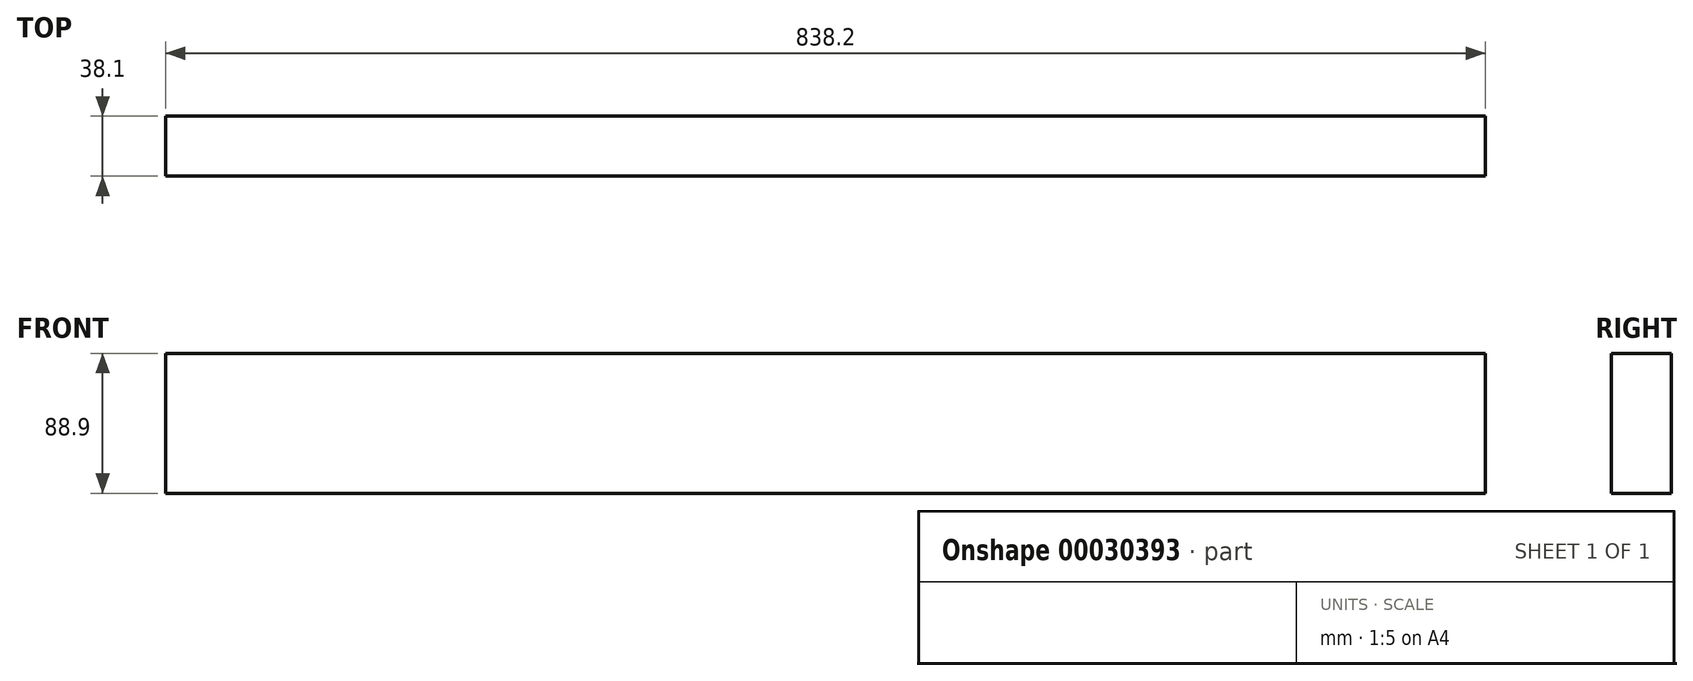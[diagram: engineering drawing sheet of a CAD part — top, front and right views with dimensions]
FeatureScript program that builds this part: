
annotation { "Feature Type Name" : "Feature", "Feature Type Description" : "" }
export const myFeature = defineFeature(function(context is Context, id is Id, definition is map)
    precondition{}
    {
        {
            var Q0;
            Q0=qCreatedBy(makeId("Front.planeOp"),FACE);
            var sketch = newSketch(context, id + "F0", { "sketchPlane" : qUnion([Q0])});
            skLineSegment(sketch, "E0.rect.bottom", {"start": v(419.1, 44.45) * mm, "end": v(-419.1, 44.45) * mm});
            skLineSegment(sketch, "E0.rect.top", {"start": v(419.1, -44.45) * mm, "end": v(-419.1, -44.45) * mm});
            skLineSegment(sketch, "E0.rect.left", {"start": v(419.1, 44.45) * mm, "end": v(419.1, -44.45) * mm});
            skLineSegment(sketch, "E0.rect.right", {"start": v(-419.1, 44.45) * mm, "end": v(-419.1, -44.45) * mm});
            skPoint(sketch, "E0.rect.middle", {"position": v(0, 0) * mm});
            skSolve(sketch);
        }
        {
            var Q0;
            Q0=makeQuery(id+"F0.imprint","IMPRINT",FACE,{"disambiguationData":[TD([[makeQuery(id+"F0.imprint","IMPRINT",EDGE,{"derivedFrom":sQuery(id+"F0.wireOp",EDGE,"E0.rect.bottom")}),1.0]])]});
            extrude(context, id + "F1", {"entities" : qUnion([Q0]), "endBound" : BoundingType.SYMMETRIC, "depth" : 38.1 * mm});
        }
    });
